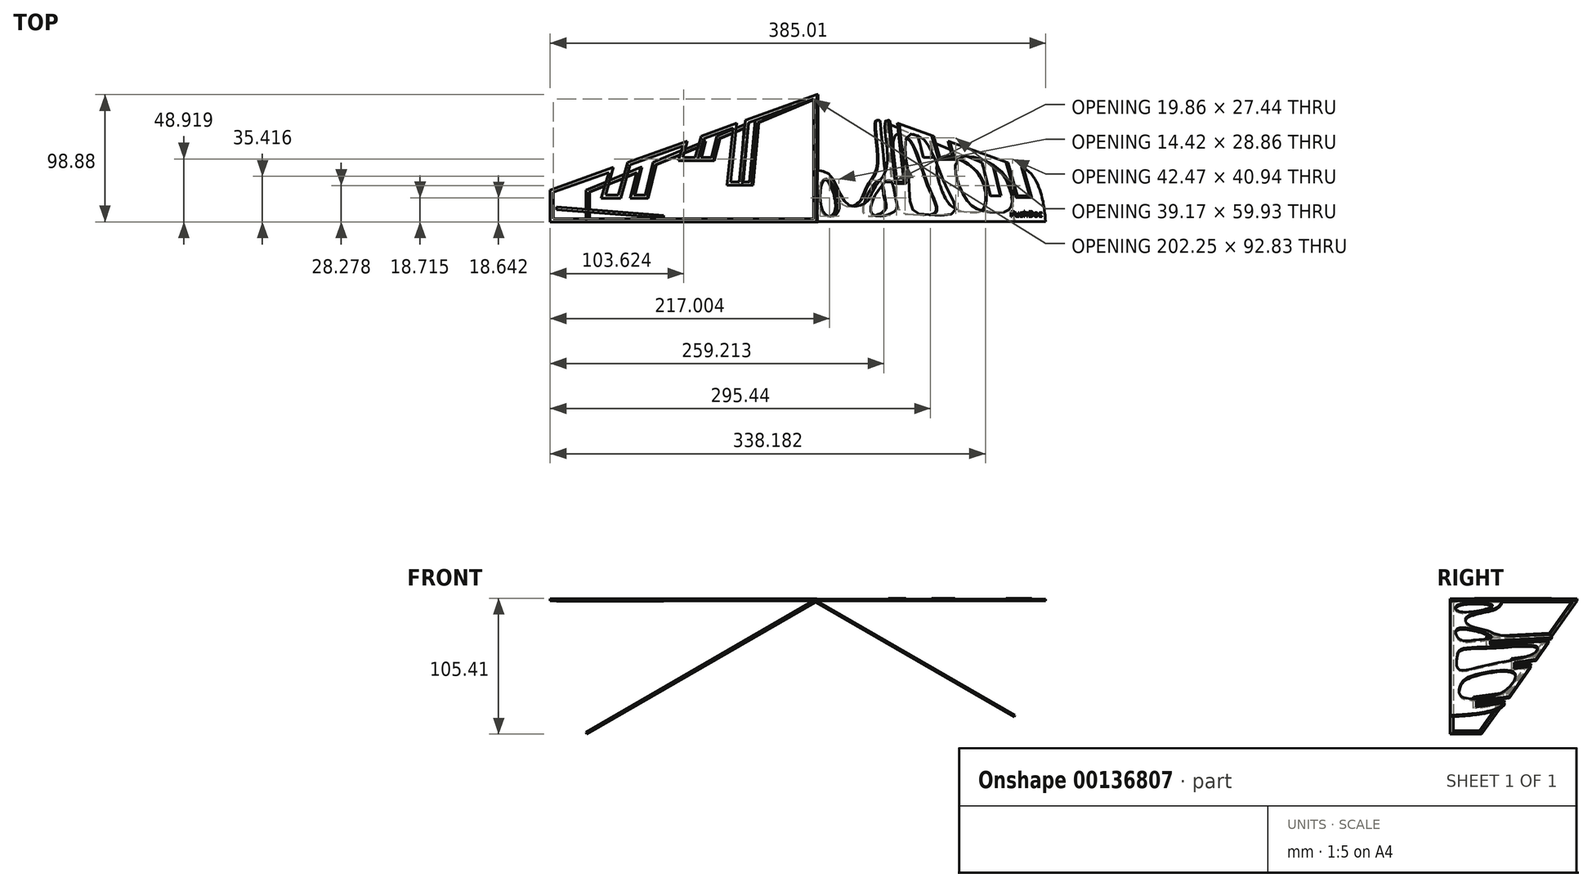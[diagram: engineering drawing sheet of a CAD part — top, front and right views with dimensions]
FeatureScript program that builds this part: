
annotation { "Feature Type Name" : "Feature", "Feature Type Description" : "" }
export const myFeature = defineFeature(function(context is Context, id is Id, definition is map)
    precondition{}
    {
        {
            var Q0;
            Q0=qCreatedBy(makeId("Top.planeOp"),FACE);
            var sketch = newSketch(context, id + "F0", { "sketchPlane" : qUnion([Q0])});
            skLineSegment(sketch, "E0", {"start": v(-207.25, 4.5) * mm, "end": v(-207.25, 29.16) * mm});
            skLineSegment(sketch, "E1", {"start": v(-207.25, 29.16) * mm, "end": v(0, 103.37) * mm});
            skLineSegment(sketch, "E2", {"start": v(0, 103.37) * mm, "end": v(0, 4.5) * mm});
            skLineSegment(sketch, "E3", {"start": v(0, 4.5) * mm, "end": v(-207.25, 4.5) * mm});
            skLineSegment(sketch, "E4", {"start": v(-154.52, 59.15) * mm, "end": v(-164.24, 25.2) * mm});
            skLineSegment(sketch, "E5", {"start": v(-164.24, 25.2) * mm, "end": v(-154.24, 25.2) * mm});
            skLineSegment(sketch, "E6", {"start": v(-154.24, 25.2) * mm, "end": v(-144.66, 59.42) * mm});
            skLineSegment(sketch, "E7", {"start": v(-144.66, 59.42) * mm, "end": v(-154.52, 59.15) * mm});
            skLineSegment(sketch, "E8", {"start": v(-104.27, 54.63) * mm, "end": v(-97.43, 78.46) * mm});
            skLineSegment(sketch, "E9", {"start": v(-97.43, 78.46) * mm, "end": v(-87.93, 78.46) * mm});
            skLineSegment(sketch, "E10", {"start": v(-87.93, 78.46) * mm, "end": v(-94.77, 54.63) * mm});
            skLineSegment(sketch, "E11", {"start": v(-94.77, 54.63) * mm, "end": v(-104.27, 54.63) * mm});
            skLineSegment(sketch, "E12", {"start": v(-67.03, 35.46) * mm, "end": v(-60.53, 35.46) * mm});
            skLineSegment(sketch, "E13", {"start": v(-60.53, 35.46) * mm, "end": v(-54.84, 90.5) * mm});
            skLineSegment(sketch, "E14", {"start": v(-54.84, 90.5) * mm, "end": v(-61.34, 90.5) * mm});
            skLineSegment(sketch, "E15", {"start": v(-61.34, 90.5) * mm, "end": v(-67.03, 35.46) * mm});
            skSolve(sketch);
        }
        {
            var Q0;
            {var subQ17=sQuery(id+"F0.wireOp",EDGE,"E0");Q0=makeQuery(id+"F0.imprint","IMPRINT",FACE,{"disambiguationData":[TD([[makeQuery(id+"F0.imprint","IMPRINT",EDGE,{"derivedFrom":subQ17}),-1.0]])]});}
            extrude(context, id + "F1", {"entities" : qUnion([Q0]), "depth" : 1.6 * mm});
        }
        {
            var Q0;
            Q0=makeQuery(id+"F1.opExtrude","CAP_FACE",FACE,{"disambiguationData":[OSD([sQuery(id+"F0.wireOp",EDGE,"E0"),sQuery(id+"F0.wireOp",EDGE,"E1"),sQuery(id+"F0.wireOp",EDGE,"E2"),sQuery(id+"F0.wireOp",EDGE,"E3"),sQuery(id+"F0.wireOp",EDGE,"E4"),sQuery(id+"F0.wireOp",EDGE,"E5"),sQuery(id+"F0.wireOp",EDGE,"E6"),sQuery(id+"F0.wireOp",EDGE,"E8"),sQuery(id+"F0.wireOp",EDGE,"E10"),sQuery(id+"F0.wireOp",EDGE,"E11"),sQuery(id+"F0.wireOp",EDGE,"E12"),sQuery(id+"F0.wireOp",EDGE,"E13"),sQuery(id+"F0.wireOp",EDGE,"E15")])],"isStart":false});
            var Q1;
            Q1=makeQuery(id+"F1.opExtrude","CAP_FACE",FACE,{"disambiguationData":[OSD([sQuery(id+"F0.wireOp",EDGE,"E0"),sQuery(id+"F0.wireOp",EDGE,"E1"),sQuery(id+"F0.wireOp",EDGE,"E2"),sQuery(id+"F0.wireOp",EDGE,"E3"),sQuery(id+"F0.wireOp",EDGE,"E4"),sQuery(id+"F0.wireOp",EDGE,"E5"),sQuery(id+"F0.wireOp",EDGE,"E6"),sQuery(id+"F0.wireOp",EDGE,"E8"),sQuery(id+"F0.wireOp",EDGE,"E10"),sQuery(id+"F0.wireOp",EDGE,"E11"),sQuery(id+"F0.wireOp",EDGE,"E12"),sQuery(id+"F0.wireOp",EDGE,"E13"),sQuery(id+"F0.wireOp",EDGE,"E15")])],"isStart":true});
            shell(context, id + "F2", {"entities" : qUnion([Q0, Q1]), "thickness" : 2.5 * mm});
        }
        {
            var Q0;
            Q0=makeQuery(id+"F1.opExtrude","SWEPT_BODY",BODY,{"disambiguationData":[OSD([sQuery(id+"F0.wireOp",EDGE,"E0"),sQuery(id+"F0.wireOp",EDGE,"E1"),sQuery(id+"F0.wireOp",EDGE,"E2"),sQuery(id+"F0.wireOp",EDGE,"E3"),sQuery(id+"F0.wireOp",EDGE,"E4"),sQuery(id+"F0.wireOp",EDGE,"E5"),sQuery(id+"F0.wireOp",EDGE,"E6"),sQuery(id+"F0.wireOp",EDGE,"E8"),sQuery(id+"F0.wireOp",EDGE,"E10"),sQuery(id+"F0.wireOp",EDGE,"E11"),sQuery(id+"F0.wireOp",EDGE,"E12"),sQuery(id+"F0.wireOp",EDGE,"E13"),sQuery(id+"F0.wireOp",EDGE,"E15")])]});
            var Q1;
            Q1=makeQuery(id+"F1.opExtrude","CAP_EDGE",EDGE,{"disambiguationData":[OSD([sQuery(id+"F0.wireOp",EDGE,"E2")])],"isStart":false});
            transform(context, id + "F3", {"entities" : qUnion([Q0]), "transformType" : TransformType.ROTATION, "transformAxis" : qUnion([Q1]), "angle" : 30 * degree, "makeCopy" : true});
        }
        {
            var Q0;
            Q0=makeQuery(id+"F1.opExtrude","CAP_FACE",FACE,{"disambiguationData":[OSD([sQuery(id+"F0.wireOp",EDGE,"E0"),sQuery(id+"F0.wireOp",EDGE,"E1"),sQuery(id+"F0.wireOp",EDGE,"E2"),sQuery(id+"F0.wireOp",EDGE,"E3"),sQuery(id+"F0.wireOp",EDGE,"E4"),sQuery(id+"F0.wireOp",EDGE,"E5"),sQuery(id+"F0.wireOp",EDGE,"E6"),sQuery(id+"F0.wireOp",EDGE,"E8"),sQuery(id+"F0.wireOp",EDGE,"E10"),sQuery(id+"F0.wireOp",EDGE,"E11"),sQuery(id+"F0.wireOp",EDGE,"E12"),sQuery(id+"F0.wireOp",EDGE,"E13"),sQuery(id+"F0.wireOp",EDGE,"E15")])],"isStart":false});
            var sketch = newSketch(context, id + "F4", { "sketchPlane" : qUnion([Q0])});
            skText(sketch, "E16", { "text": "PushDoctor", "fontName": "OpenSans-Regular.ttf"});
            const initialGuessF4  = {"E16": [-0.20136, 0.00818, 1, 0, 0.00977]};
            skSetInitialGuess(sketch, initialGuessF4);
            skSolve(sketch);
        }
        {
            var Q0;
            Q0 = qSketchRegion(id + "F4", true);
            extrude(context, id + "F5", {"entities" : qUnion([Q0]), "operationType" : NewBodyOperationType.REMOVE, "oppositeDirection" : true, "depth" : 25 * mm});
        }
        {
            var Q0;
            {var subQ0=sQuery(id+"F0.wireOp",EDGE,"E5");var subQ1=sQuery(id+"F0.wireOp",EDGE,"E6");var subQ2=sQuery(id+"F0.wireOp",EDGE,"E1");var subQ3=sQuery(id+"F0.wireOp",EDGE,"E8");var subQ4=sQuery(id+"F0.wireOp",EDGE,"E12");var subQ5=sQuery(id+"F0.wireOp",EDGE,"E11");var subQ6=sQuery(id+"F0.wireOp",EDGE,"E10");var subQ7=sQuery(id+"F0.wireOp",EDGE,"E15");var subQ8=sQuery(id+"F0.wireOp",EDGE,"E0");var subQ9=sQuery(id+"F0.wireOp",EDGE,"E4");var subQ10=sQuery(id+"F0.wireOp",EDGE,"E2");var subQ11=sQuery(id+"F0.wireOp",EDGE,"E13");var subQ12=sQuery(id+"F0.wireOp",EDGE,"E3");Q0=makeQuery(id+"F5.boolean.opBoolean","SPLIT",FACE,{"disambiguationData":[TD([makeQuery(id+"F1.opExtrude","SWEPT_FACE",FACE,{"disambiguationData":[OSD([subQ8])]})])],"derivedFrom":makeQuery(id+"F1.opExtrude","CAP_FACE",FACE,{"disambiguationData":[OSD([subQ8,subQ2,subQ10,subQ12,subQ9,subQ0,subQ1,subQ3,subQ6,subQ5,subQ4,subQ11,subQ7])],"isStart":false})});}
            var sketch = newSketch(context, id + "F6", { "sketchPlane" : qUnion([Q0])});
            skLineSegment(sketch, "E17", {"start": v(-202.2, 15.97) * mm, "end": v(-119.06, 9.54) * mm});
            skLineSegment(sketch, "E18", {"start": v(-119.06, 9.54) * mm, "end": v(-119.06, 7.54) * mm});
            skLineSegment(sketch, "E19", {"start": v(-119.06, 7.54) * mm, "end": v(-202.2, 13.97) * mm});
            skLineSegment(sketch, "E20", {"start": v(-202.2, 13.97) * mm, "end": v(-202.2, 15.97) * mm});
            skSolve(sketch);
        }
        {
            var Q0;
            Q0 = qSketchRegion(id + "F6", true);
            extrude(context, id + "F7", {"entities" : qUnion([Q0]), "depth" : 1 * mm});
        }
        {
            var Q0;
            Q0=makeQuery(id+"F7.opExtrude","SWEPT_BODY",BODY,{"disambiguationData":[OSD([sQuery(id+"F6.wireOp",EDGE,"E17"),sQuery(id+"F6.wireOp",EDGE,"E18"),sQuery(id+"F6.wireOp",EDGE,"E19"),sQuery(id+"F6.wireOp",EDGE,"E20")])]});
            transform(context, id + "F8", {"entities" : qUnion([Q0]), "transformType" : TransformType.TRANSLATION_3D, "dx" : 0 * mm, "dy" : 0 * mm, "dz" : -2 * mm, "makeCopy" : false});
        }
        {
            var Q0;
            Q0=qCreatedBy(makeId("Top.planeOp"),FACE);
            var sketch = newSketch(context, id + "F9", { "sketchPlane" : qUnion([Q0])});
            skLineSegment(sketch, "E21", {"start": v(158.93, 46.94) * mm, "end": v(165.22, 24.82) * mm});
            skLineSegment(sketch, "E22", {"start": v(165.22, 24.82) * mm, "end": v(155.72, 24.82) * mm});
            skLineSegment(sketch, "E23", {"start": v(155.72, 24.82) * mm, "end": v(148.43, 50.45) * mm});
            skLineSegment(sketch, "E24", {"start": v(101.83, 67.1) * mm, "end": v(105.47, 54.41) * mm});
            skLineSegment(sketch, "E25", {"start": v(105.47, 54.41) * mm, "end": v(95.47, 54.41) * mm});
            skLineSegment(sketch, "E26", {"start": v(95.47, 54.41) * mm, "end": v(90.67, 71.13) * mm});
            skLineSegment(sketch, "E27", {"start": v(62.6, 81.15) * mm, "end": v(67.57, 35.52) * mm});
            skLineSegment(sketch, "E28", {"start": v(67.57, 35.52) * mm, "end": v(62.07, 35.52) * mm});
            skLineSegment(sketch, "E29", {"start": v(62.07, 35.52) * mm, "end": v(56.87, 83.16) * mm});
            skLineSegment(sketch, "E30", {"start": v(0, 4.75) * mm, "end": v(0, 44.75) * mm});
            skFitSpline(sketch, "E31", {"points": [v(0, 44.75) * mm, v(12.07, 38.51) * mm, v(23.73, 18.17) * mm, v(35.31, 17.87) * mm, v(40.95, 22.9) * mm, v(46.14, 33.11) * mm, v(54.68, 48.3) * mm, v(53.26, 83.1) * mm, v(56.87, 83.16) * mm], "startDerivative": vector(135.94, -17.6) * mm, "endDerivative": vector(60.2, -1.37) * mm});
            skLineSegment(sketch, "E32", {"start": v(62.6, 81.15) * mm, "end": v(90.67, 71.13) * mm});
            skLineSegment(sketch, "E33", {"start": v(101.83, 67.1) * mm, "end": v(148.43, 50.45) * mm});
            skLineSegment(sketch, "E34", {"start": v(0, 4.75) * mm, "end": v(177.76, 4.75) * mm});
            skFitSpline(sketch, "E35", {"points": [v(177.76, 4.75) * mm, v(175.18, 22.35) * mm, v(158.93, 46.94) * mm], "startDerivative": vector(-7.31, 61.42) * mm, "endDerivative": vector(-57.18, 21.84) * mm});
            skFitSpline(sketch, "E36", {"points": [v(86.84, 9.94) * mm, v(74.19, 14.2) * mm, v(71.38, 37.93) * mm, v(68.83, 55.24) * mm, v(70.99, 71.99) * mm, v(80.9, 70.16) * mm, v(86.98, 63.1) * mm, v(92.8, 50.64) * mm, v(102.24, 28.08) * mm, v(107.2, 12.25) * mm, v(86.84, 9.94) * mm]});
            skFitSpline(sketch, "E37", {"points": [v(109.71, 53.24) * mm, v(115.02, 23.43) * mm, v(128.73, 13.11) * mm, v(147.52, 12.84) * mm, v(152.1, 21.26) * mm, v(142.95, 44.24) * mm, v(109.71, 53.24) * mm]});
            skFitSpline(sketch, "E38", {"points": [v(6.94, 37.63) * mm, v(5.45, 11.58) * mm, v(16.93, 13.14) * mm, v(6.94, 37.63) * mm]});
            skFitSpline(sketch, "E39", {"points": [v(55.77, 36.85) * mm, v(42.17, 11.6) * mm, v(60.39, 12.73) * mm, v(61.08, 23.07) * mm, v(55.77, 36.85) * mm]});
            skLineSegment(sketch, "E40.0", {"start": v(67.77, 40.52) * mm, "end": v(62.27, 40.52) * mm});
            skLineSegment(sketch, "E41.0", {"start": v(60.72, 34.02) * mm, "end": v(55.34, 83.42) * mm});
            skLineSegment(sketch, "E41.1", {"start": v(69.24, 34.02) * mm, "end": v(60.72, 34.02) * mm});
            skLineSegment(sketch, "E41.2", {"start": v(64.16, 80.59) * mm, "end": v(69.24, 34.02) * mm});
            skLineSegment(sketch, "E42.0", {"start": v(94.34, 52.91) * mm, "end": v(88.93, 71.75) * mm});
            skLineSegment(sketch, "E42.1", {"start": v(107.47, 52.91) * mm, "end": v(94.34, 52.91) * mm});
            skLineSegment(sketch, "E42.2", {"start": v(103.57, 66.47) * mm, "end": v(107.47, 52.91) * mm});
            skLineSegment(sketch, "E43.0", {"start": v(154.6, 23.32) * mm, "end": v(146.7, 51.07) * mm});
            skLineSegment(sketch, "E43.1", {"start": v(167.21, 23.32) * mm, "end": v(154.6, 23.32) * mm});
            skLineSegment(sketch, "E43.2", {"start": v(160.71, 46.15) * mm, "end": v(167.21, 23.32) * mm});
            skSolve(sketch);
        }
        {
            var Q0;
            {var subQ4=sQuery(id+"F9.wireOp",EDGE,"E30");Q0=makeQuery(id+"F9.imprint","IMPRINT",FACE,{"disambiguationData":[TD([[makeQuery(id+"F9.imprint","IMPRINT",EDGE,{"derivedFrom":subQ4}),-1.0]])]});}
            var Q1;
            {var subQ4=sQuery(id+"F9.wireOp",EDGE,"E24");Q1=makeQuery(id+"F9.imprint","IMPRINT",FACE,{"disambiguationData":[TD([[makeQuery(id+"F9.imprint","IMPRINT",EDGE,{"derivedFrom":subQ4}),1.0]])]});}
            var Q2;
            {var subQ3=sQuery(id+"F9.wireOp",EDGE,"E28");Q2=makeQuery(id+"F9.imprint","IMPRINT",FACE,{"disambiguationData":[TD([[makeQuery(id+"F9.imprint","IMPRINT",EDGE,{"derivedFrom":subQ3}),1.0]])]});}
            var Q3;
            {var subQ3=sQuery(id+"F9.wireOp",EDGE,"E21");Q3=makeQuery(id+"F9.imprint","IMPRINT",FACE,{"disambiguationData":[TD([[makeQuery(id+"F9.imprint","IMPRINT",EDGE,{"derivedFrom":subQ3}),1.0]])]});}
            extrude(context, id + "F10", {"entities" : qUnion([Q0, Q1, Q2, Q3]), "depth" : 1.4 * mm});
        }
        {
            var Q0;
            {var subQ3=sQuery(id+"F9.wireOp",EDGE,"E28");Q0=makeQuery(id+"F9.imprint","IMPRINT",FACE,{"disambiguationData":[TD([[makeQuery(id+"F9.imprint","IMPRINT",EDGE,{"derivedFrom":subQ3}),1.0]])]});}
            var Q1;
            {var subQ4=sQuery(id+"F9.wireOp",EDGE,"E24");Q1=makeQuery(id+"F9.imprint","IMPRINT",FACE,{"disambiguationData":[TD([[makeQuery(id+"F9.imprint","IMPRINT",EDGE,{"derivedFrom":subQ4}),1.0]])]});}
            var Q2;
            {var subQ3=sQuery(id+"F9.wireOp",EDGE,"E21");Q2=makeQuery(id+"F9.imprint","IMPRINT",FACE,{"disambiguationData":[TD([[makeQuery(id+"F9.imprint","IMPRINT",EDGE,{"derivedFrom":subQ3}),1.0]])]});}
            extrude(context, id + "F11", {"entities" : qUnion([Q0, Q1, Q2]), "depth" : 1 * mm, "hasDraft" : true, "draftAngle" : 10 * degree, "draftPullDirection" : true});
        }
        {
            var Q0;
            Q0=makeQuery(id+"F11.opExtrude","SWEPT_BODY",BODY,{"disambiguationData":[OSD([sQuery(id+"F9.wireOp",EDGE,"E21"),sQuery(id+"F9.wireOp",EDGE,"E22"),sQuery(id+"F9.wireOp",EDGE,"E23"),sQuery(id+"F9.wireOp",EDGE,"E33"),sQuery(id+"F9.wireOp",EDGE,"E35"),sQuery(id+"F9.wireOp",EDGE,"E43.0"),sQuery(id+"F9.wireOp",EDGE,"E43.1"),sQuery(id+"F9.wireOp",EDGE,"E43.2")])]});
            var Q1;
            Q1=makeQuery(id+"F11.opExtrude","SWEPT_BODY",BODY,{"disambiguationData":[OSD([sQuery(id+"F9.wireOp",EDGE,"E24"),sQuery(id+"F9.wireOp",EDGE,"E25"),sQuery(id+"F9.wireOp",EDGE,"E26"),sQuery(id+"F9.wireOp",EDGE,"E32"),sQuery(id+"F9.wireOp",EDGE,"E33"),sQuery(id+"F9.wireOp",EDGE,"E42.0"),sQuery(id+"F9.wireOp",EDGE,"E42.1"),sQuery(id+"F9.wireOp",EDGE,"E42.2")])]});
            var Q2;
            Q2=makeQuery(id+"F11.opExtrude","SWEPT_BODY",BODY,{"disambiguationData":[OSD([sQuery(id+"F9.wireOp",EDGE,"E27"),sQuery(id+"F9.wireOp",EDGE,"E28"),sQuery(id+"F9.wireOp",EDGE,"E29"),sQuery(id+"F9.wireOp",EDGE,"E31"),sQuery(id+"F9.wireOp",EDGE,"E32"),sQuery(id+"F9.wireOp",EDGE,"E41.0"),sQuery(id+"F9.wireOp",EDGE,"E41.1"),sQuery(id+"F9.wireOp",EDGE,"E41.2")])]});
            transform(context, id + "F12", {"entities" : qUnion([Q0, Q1, Q2]), "transformType" : TransformType.TRANSLATION_3D, "dx" : 0 * mm, "dy" : 0 * mm, "dz" : 1 * mm, "makeCopy" : false});
        }
        {
            var Q0;
            Q0=makeQuery(id+"F10.opExtrude","CAP_FACE",FACE,{"disambiguationData":[OSD([sQuery(id+"F9.wireOp",EDGE,"E21"),sQuery(id+"F9.wireOp",EDGE,"E22"),sQuery(id+"F9.wireOp",EDGE,"E23"),sQuery(id+"F9.wireOp",EDGE,"E24"),sQuery(id+"F9.wireOp",EDGE,"E25"),sQuery(id+"F9.wireOp",EDGE,"E26"),sQuery(id+"F9.wireOp",EDGE,"E27"),sQuery(id+"F9.wireOp",EDGE,"E28"),sQuery(id+"F9.wireOp",EDGE,"E29"),sQuery(id+"F9.wireOp",EDGE,"E30"),sQuery(id+"F9.wireOp",EDGE,"E31"),sQuery(id+"F9.wireOp",EDGE,"E32"),sQuery(id+"F9.wireOp",EDGE,"E33"),sQuery(id+"F9.wireOp",EDGE,"E34"),sQuery(id+"F9.wireOp",EDGE,"E35"),sQuery(id+"F9.wireOp",EDGE,"E36"),sQuery(id+"F9.wireOp",EDGE,"E37"),sQuery(id+"F9.wireOp",EDGE,"E38"),sQuery(id+"F9.wireOp",EDGE,"E39")])],"isStart":false});
            var sketch = newSketch(context, id + "F13", { "sketchPlane" : qUnion([Q0])});
            skText(sketch, "E44", { "text": "PushDoc", "fontName": "OpenSans-Regular.ttf"});
            const initialGuessF13  = {"E44": [0.15028, 0.00849, 1, 0, 0.00432]};
            skSetInitialGuess(sketch, initialGuessF13);
            skSolve(sketch);
        }
        {
            var Q0;
            Q0=makeQuery(id+"F10.opExtrude","SWEPT_BODY",BODY,{"disambiguationData":[OSD([sQuery(id+"F9.wireOp",EDGE,"E21"),sQuery(id+"F9.wireOp",EDGE,"E22"),sQuery(id+"F9.wireOp",EDGE,"E23"),sQuery(id+"F9.wireOp",EDGE,"E24"),sQuery(id+"F9.wireOp",EDGE,"E25"),sQuery(id+"F9.wireOp",EDGE,"E26"),sQuery(id+"F9.wireOp",EDGE,"E27"),sQuery(id+"F9.wireOp",EDGE,"E28"),sQuery(id+"F9.wireOp",EDGE,"E29"),sQuery(id+"F9.wireOp",EDGE,"E30"),sQuery(id+"F9.wireOp",EDGE,"E31"),sQuery(id+"F9.wireOp",EDGE,"E32"),sQuery(id+"F9.wireOp",EDGE,"E33"),sQuery(id+"F9.wireOp",EDGE,"E34"),sQuery(id+"F9.wireOp",EDGE,"E35"),sQuery(id+"F9.wireOp",EDGE,"E36"),sQuery(id+"F9.wireOp",EDGE,"E37"),sQuery(id+"F9.wireOp",EDGE,"E38"),sQuery(id+"F9.wireOp",EDGE,"E39")])]});
            var Q1;
            {var subQ4=sQuery(id+"F9.wireOp",EDGE,"E30");Q1=makeQuery(id+"F9.imprint","IMPRINT",FACE,{"disambiguationData":[TD([[makeQuery(id+"F9.imprint","IMPRINT",EDGE,{"derivedFrom":subQ4}),-1.0]])]});}
            mirror(context, id + "F14", {"entities" : qUnion([Q0]), "mirrorPlane" : qUnion([Q1])});
        }
        {
            var Q0;
            Q0 = qSketchRegion(id + "F13", true);
            extrude(context, id + "F15", {"entities" : qUnion([Q0]), "operationType" : NewBodyOperationType.REMOVE, "oppositeDirection" : true, "depth" : .4 * mm});
        }
        {
            var Q0;
            Q0=makeQuery(id+"F14.opPattern","COPY",BODY,{"derivedFrom":makeQuery(id+"F10.opExtrude","SWEPT_BODY",BODY,{"disambiguationData":[OSD([sQuery(id+"F9.wireOp",EDGE,"E21"),sQuery(id+"F9.wireOp",EDGE,"E22"),sQuery(id+"F9.wireOp",EDGE,"E23"),sQuery(id+"F9.wireOp",EDGE,"E24"),sQuery(id+"F9.wireOp",EDGE,"E25"),sQuery(id+"F9.wireOp",EDGE,"E26"),sQuery(id+"F9.wireOp",EDGE,"E27"),sQuery(id+"F9.wireOp",EDGE,"E28"),sQuery(id+"F9.wireOp",EDGE,"E29"),sQuery(id+"F9.wireOp",EDGE,"E30"),sQuery(id+"F9.wireOp",EDGE,"E31"),sQuery(id+"F9.wireOp",EDGE,"E32"),sQuery(id+"F9.wireOp",EDGE,"E33"),sQuery(id+"F9.wireOp",EDGE,"E34"),sQuery(id+"F9.wireOp",EDGE,"E35"),sQuery(id+"F9.wireOp",EDGE,"E36"),sQuery(id+"F9.wireOp",EDGE,"E37"),sQuery(id+"F9.wireOp",EDGE,"E38"),sQuery(id+"F9.wireOp",EDGE,"E39")])]}),"instanceName":"1"});
            var Q1;
            Q1=sQuery(id+"F0.wireOp",EDGE,"E2");
            transform(context, id + "F16", {"entities" : qUnion([Q0]), "transformType" : TransformType.ROTATION, "transformAxis" : qUnion([Q1]), "angle" : 30 * degree, "oppositeDirection" : true, "makeCopy" : false});
        }
        {
            var Q0;
            Q0=qCreatedBy(makeId("Front.planeOp"),FACE);
            var sketch = newSketch(context, id + "F17", { "sketchPlane" : qUnion([Q0])});
            skArc(sketch, "E45", {"start": v(0, 1.4) * mm, "mid": v(-1.35, 0.36) * mm, "end": v(-0.7, -1.21) * mm});
            skArc(sketch, "E46", {"start": v(0, 0.9) * mm, "mid": v(-0.87, 0.23) * mm, "end": v(-0.45, -0.78) * mm});
            skLineSegment(sketch, "E47", {"start": v(0, 1.4) * mm, "end": v(0, 0) * mm});
            skLineSegment(sketch, "E48", {"start": v(-0.74, -1.28) * mm, "end": v(0, 0) * mm});
            skSolve(sketch);
        }
        {
            var Q0;
            {var subQ0=sQuery(id+"F17.wireOp",EDGE,"E45");Q0=makeQuery(id+"F17.imprint","IMPRINT",FACE,{"disambiguationData":[TD([[makeQuery(id+"F17.imprint","IMPRINT",EDGE,{"derivedFrom":subQ0}),1.0]])]});}
            extrude(context, id + "F18", {"entities" : qUnion([Q0]), "oppositeDirection" : true, "depth" : 38 * mm});
        }
        {
            var Q0;
            Q0=makeQuery(id+"F18.opExtrude","SWEPT_BODY",BODY,{"disambiguationData":[OSD([sQuery(id+"F17.wireOp",EDGE,"E45"),sQuery(id+"F17.wireOp",EDGE,"E46"),sQuery(id+"F17.wireOp",EDGE,"E47"),sQuery(id+"F17.wireOp",EDGE,"E48")])]});
            transform(context, id + "F19", {"entities" : qUnion([Q0]), "transformType" : TransformType.TRANSLATION_3D, "dx" : 0 * mm, "dy" : 4.75 * mm, "dz" : 0 * mm, "makeCopy" : false});
        }
        {
            var Q0;
            Q0=makeQuery(id+"F18.opExtrude","SWEPT_BODY",BODY,{"disambiguationData":[OSD([sQuery(id+"F17.wireOp",EDGE,"E45"),sQuery(id+"F17.wireOp",EDGE,"E46"),sQuery(id+"F17.wireOp",EDGE,"E47"),sQuery(id+"F17.wireOp",EDGE,"E48")])]});
            transform(context, id + "F20", {"entities" : qUnion([Q0]), "transformType" : TransformType.TRANSLATION_3D, "dx" : 0.12 * mm, "dy" : 0 * mm, "dz" : 0 * mm, "makeCopy" : false});
        }
    });
